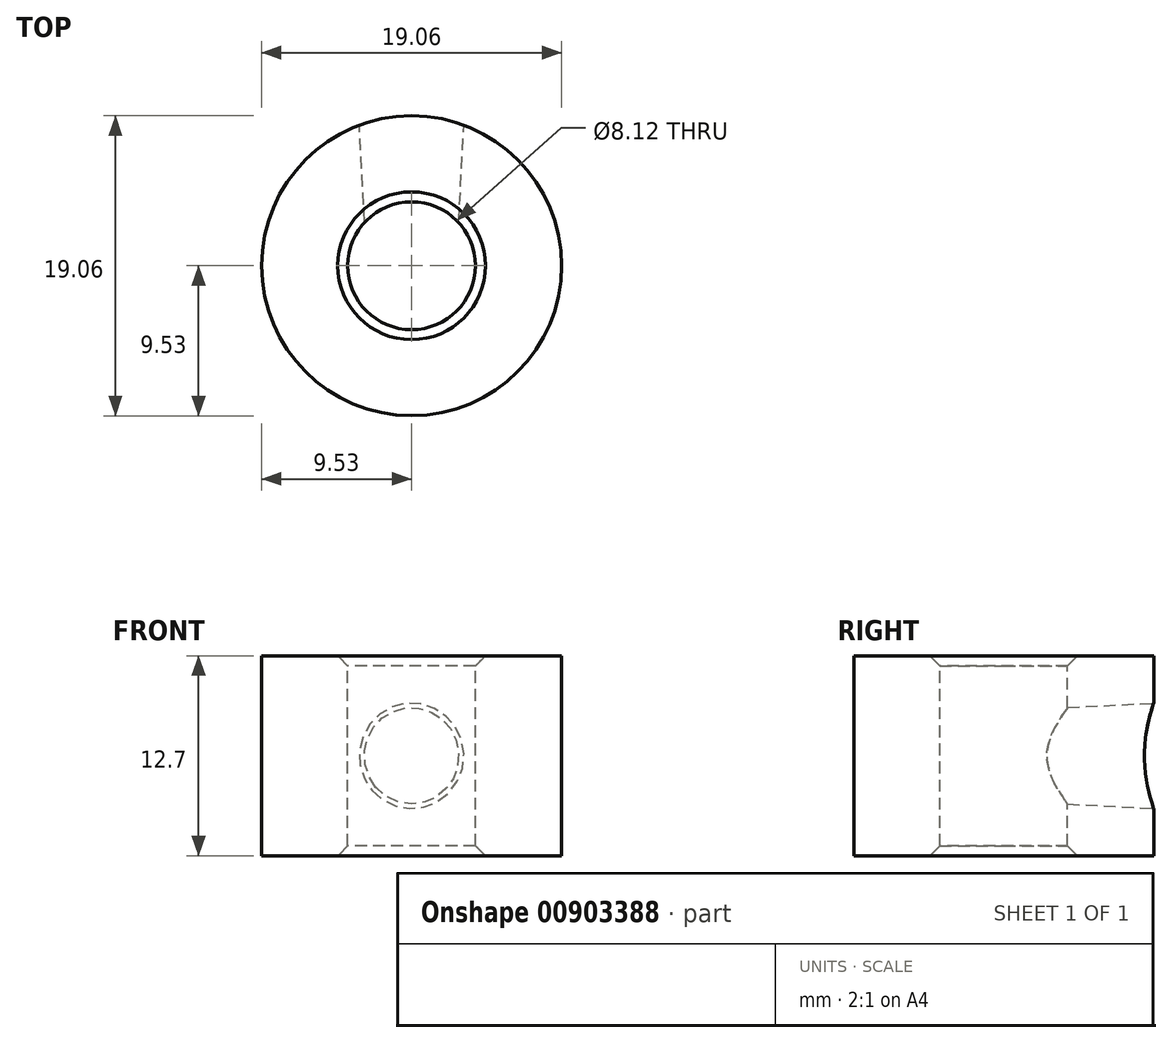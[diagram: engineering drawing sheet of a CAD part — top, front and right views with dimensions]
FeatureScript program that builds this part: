
annotation { "Feature Type Name" : "Feature", "Feature Type Description" : "" }
export const myFeature = defineFeature(function(context is Context, id is Id, definition is map)
    precondition{}
    {
        {
            var Q0;
            Q0=qCreatedBy(makeId("Top.planeOp"),FACE);
            var sketch = newSketch(context, id + "F0", { "sketchPlane" : qUnion([Q0])});
            skCircle(sketch, "E0", {"center": v(0, 0) * mm, "radius": 9.53 * mm});
            skSolve(sketch);
        }
        {
            var Q0;
            Q0=makeQuery(id+"F0.imprint","IMPRINT",FACE,{"disambiguationData":[TD([[makeQuery(id+"F0.imprint","IMPRINT",EDGE,{"derivedFrom":sQuery(id+"F0.wireOp",EDGE,"E0")}),1.0]])]});
            extrude(context, id + "F1", {"entities" : qUnion([Q0]), "endBound" : BoundingType.SYMMETRIC, "depth" : 12.7 * mm, "offsetDistance" : 25.4 * mm});
        }
        {
            var Q0;
            Q0=qCreatedBy(makeId("Top.planeOp"),FACE);
            var sketch = newSketch(context, id + "F2", { "sketchPlane" : qUnion([Q0])});
            skCircle(sketch, "E1", {"center": v(0, 0) * mm, "radius": 4.06 * mm});
            skSolve(sketch);
        }
        {
            var Q0;
            Q0=qSketchRegion(id+"F2",true);
            extrude(context, id + "F3", {"entities" : qUnion([Q0]), "operationType" : NewBodyOperationType.REMOVE, "endBound" : BoundingType.SYMMETRIC, "oppositeDirection" : true, "depth" : 25.4 * mm, "offsetDistance" : 25.4 * mm});
        }
        {
            var Q0;
            Q0=qCreatedBy(makeId("Front.planeOp"),FACE);
            var sketch = newSketch(context, id + "F4", { "sketchPlane" : qUnion([Q0])});
            skCircle(sketch, "E2", {"center": v(0, 0) * mm, "radius": 2.85 * mm});
            skSolve(sketch);
        }
        {
            var Q0;
            Q0=qSketchRegion(id+"F4",true);
            extrude(context, id + "F5", {"entities" : qUnion([Q0]), "operationType" : NewBodyOperationType.REMOVE, "endBound" : BoundingType.THROUGH_ALL, "oppositeDirection" : true, "depth" : 25.4 * mm, "offsetDistance" : 25.4 * mm, "hasDraft" : true, "draftAngle" : 3 * degree});
        }
        {
            var Q0;
            Q0=makeQuery(id+"F3.boolean.opBoolean","INTERSECT",EDGE,{"derivedFrom":[makeQuery(id+"F1.opExtrude","CAP_FACE",FACE,{"disambiguationData":[OSD([sQuery(id+"F0.wireOp",EDGE,"E0")])],"isStart":true}),makeQuery(id+"F3.opExtrude","SWEPT_FACE",FACE,{"disambiguationData":[OSD([sQuery(id+"F2.wireOp",EDGE,"E1")])]})]});
            var Q1;
            Q1=makeQuery(id+"F3.boolean.opBoolean","INTERSECT",EDGE,{"derivedFrom":[makeQuery(id+"F1.opExtrude","CAP_FACE",FACE,{"disambiguationData":[OSD([sQuery(id+"F0.wireOp",EDGE,"E0")])],"isStart":false}),makeQuery(id+"F3.opExtrude","SWEPT_FACE",FACE,{"disambiguationData":[OSD([sQuery(id+"F2.wireOp",EDGE,"E1")])]})]});
            chamfer(context, id + "F6", {"entities" : qUnion([Q0, Q1]), "width" : 0.64 * mm, "tangentPropagation" : true});
        }
    });
